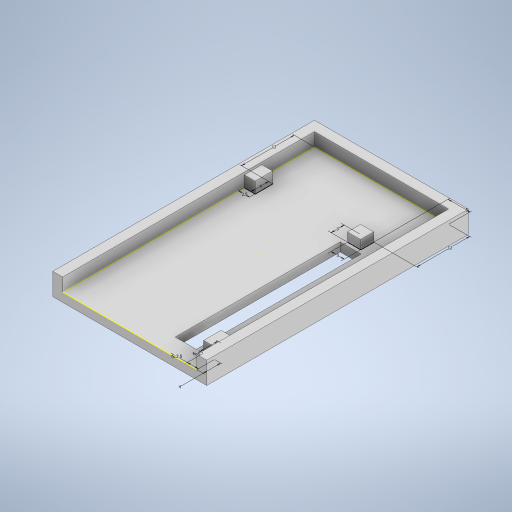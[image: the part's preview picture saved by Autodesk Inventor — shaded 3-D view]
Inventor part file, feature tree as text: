
AUTODESK INVENTOR PART (.ipt)
format: ipt  version: 2024 (Build 280153000, 153)  size: 294,912 bytes
history: native  units: in
note: dims shown in document units (in); Inventor stores cm internally (conversion verified against a paired STEP export)
features: extrude x5, sketch x4
ambient origin geometry x8: Origin, YZ Plane, XZ Plane, XY Plane, X Axis, Y Axis, Z Axis, Center Point
bodies: Solid1 (feature_tree)
feature tree (9):
  extrude  "Extrusion1"  Depth=1.378in
  extrude  "Extrusion2"  Depth=0.0886in
  sketch  "Sketch3"  dims[d5=0.0886in d6=0.0886in]
  extrude  "Extrusion3"  Depth=0.0886in
  extrude  "Extrusion4"  Depth=0.1181in
  extrude  "Extrusion5"  Depth=0.1181in
  sketch  "Sketch1"  dims[d0=2.3425in d1=1.378in]
  sketch  "Sketch2"  dims[d2=0.1969in d3=0.0in d4=0.0886in]
  sketch  "Sketch4"  dims[d7=0.1181in d8=0.0in d9=0.1181in d10=0.1181in d19=0.0787in d20=0.0in d21=0.4724in d22=0.1969in d23=0.0984in d24=0.1575in d25=0.1575in d26=0.0984in d27=0.4724in d28=0.1575in d29=0.0984in d30=0.0in d31=0.0984in d32=0.0in]
